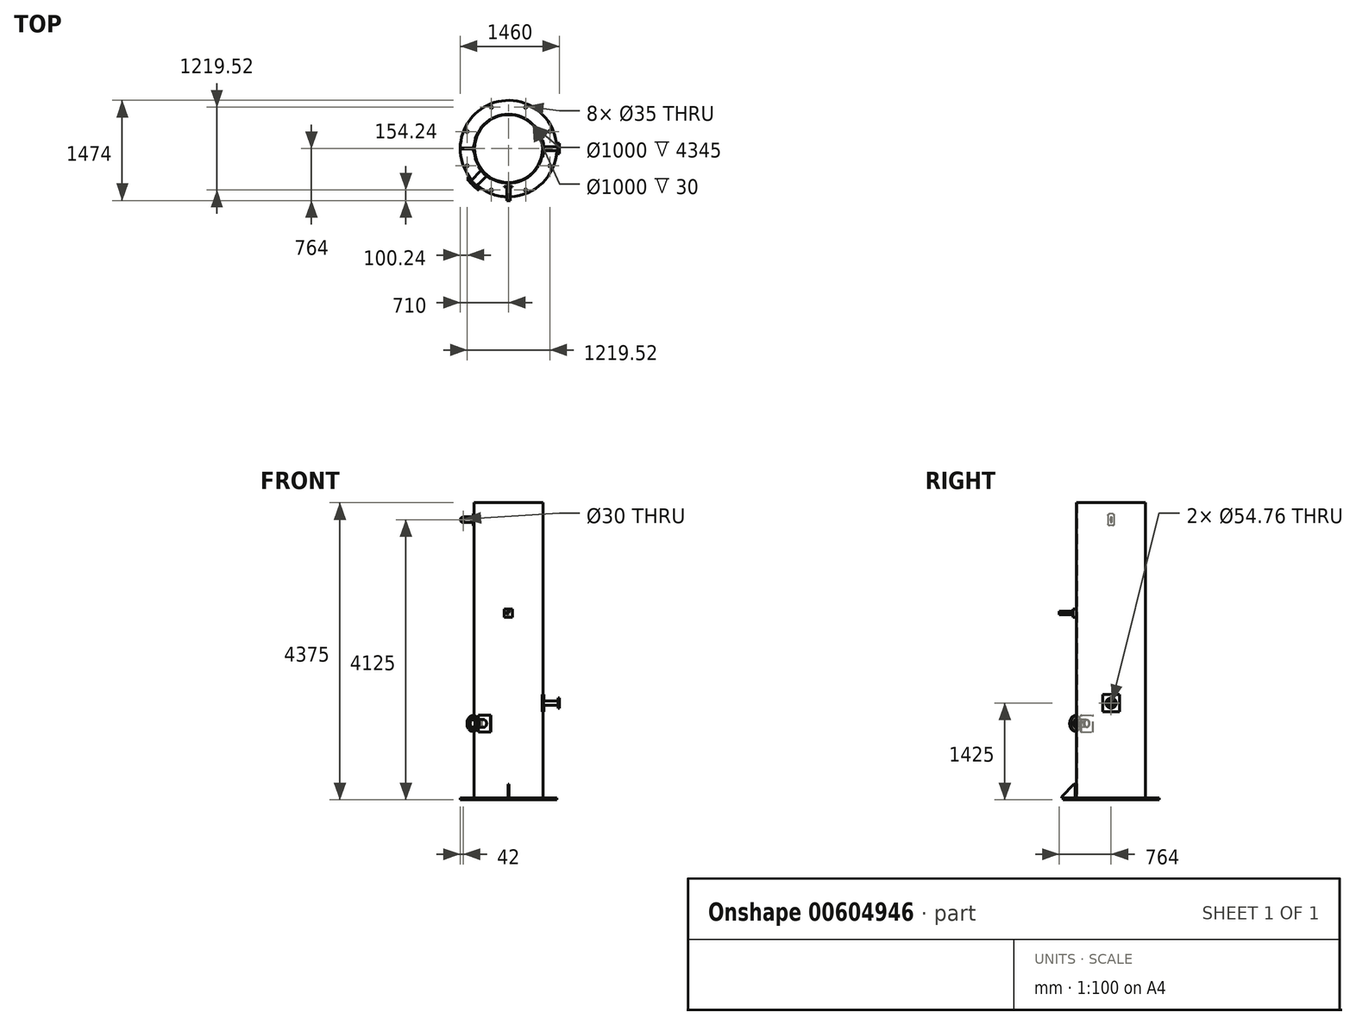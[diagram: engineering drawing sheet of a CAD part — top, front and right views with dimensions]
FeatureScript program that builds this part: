
annotation { "Feature Type Name" : "Feature", "Feature Type Description" : "" }
export const myFeature = defineFeature(function(context is Context, id is Id, definition is map)
    precondition{}
    {
        {
            var Q0;
            Q0=qCreatedBy(makeId("Top.planeOp"),FACE);
            var sketch = newSketch(context, id + "F0", { "sketchPlane" : qUnion([Q0])});
            skCircle(sketch, "E0", {"center": v(0, 0) * mm, "radius": 710 * mm});
            skCircle(sketch, "E1", {"center": v(0, 0) * mm, "radius": 660 * mm, "construction": true});
            skCircle(sketch, "E2", {"center": v(-609.76, 252.57) * mm, "radius": 17.5 * mm});
            skCircle(sketch, "E3.1.0", {"center": v(-252.57, 609.76) * mm, "radius": 17.5 * mm});
            skCircle(sketch, "E3.2.0", {"center": v(252.57, 609.76) * mm, "radius": 17.5 * mm});
            skCircle(sketch, "E3.3.0", {"center": v(609.76, 252.57) * mm, "radius": 17.5 * mm});
            skCircle(sketch, "E3.4.0", {"center": v(609.76, -252.57) * mm, "radius": 17.5 * mm});
            skCircle(sketch, "E3.5.0", {"center": v(252.57, -609.76) * mm, "radius": 17.5 * mm});
            skCircle(sketch, "E3.6.0", {"center": v(-252.57, -609.76) * mm, "radius": 17.5 * mm});
            skCircle(sketch, "E3.7.0", {"center": v(-609.76, -252.57) * mm, "radius": 17.5 * mm});
            skLineSegment(sketch, "E3.anchor1", {"start": v(0, 0) * mm, "end": v(-609.76, 252.57) * mm, "construction": true});
            skLineSegment(sketch, "E3.anchor2", {"start": v(0, 0) * mm, "end": v(-609.76, -252.57) * mm, "construction": true});
            skCircle(sketch, "E4", {"center": v(0, 0) * mm, "radius": 500 * mm});
            skSolve(sketch);
        }
        {
            var Q0;
            Q0=makeQuery(id+"F0.imprint","IMPRINT",FACE,{"disambiguationData":[TD([[makeQuery(id+"F0.imprint","IMPRINT",EDGE,{"derivedFrom":sQuery(id+"F0.wireOp",EDGE,"E0")}),1.0]])]});
            extrude(context, id + "F1", {"entities" : qUnion([Q0]), "depth" : 30 * mm, "offsetDistance" : 25 * mm});
        }
        {
            var Q0;
            Q0=makeQuery(id+"F1.opExtrude","CAP_FACE",FACE,{"disambiguationData":[OSD([sQuery(id+"F0.wireOp",EDGE,"E0"),sQuery(id+"F0.wireOp",EDGE,"E2"),sQuery(id+"F0.wireOp",EDGE,"E3.1.0"),sQuery(id+"F0.wireOp",EDGE,"E3.2.0"),sQuery(id+"F0.wireOp",EDGE,"E3.3.0"),sQuery(id+"F0.wireOp",EDGE,"E3.4.0"),sQuery(id+"F0.wireOp",EDGE,"E3.5.0"),sQuery(id+"F0.wireOp",EDGE,"E3.6.0"),sQuery(id+"F0.wireOp",EDGE,"E3.7.0"),sQuery(id+"F0.wireOp",EDGE,"E4")])],"isStart":false});
            var sketch = newSketch(context, id + "F2", { "sketchPlane" : qUnion([Q0])});
            skCircle(sketch, "E5", {"center": v(0, 0) * mm, "radius": 508 * mm});
            skCircle(sketch, "E6", {"center": v(0, 0) * mm, "radius": 498.5 * mm});
            skSolve(sketch);
        }
        {
            var Q0;
            Q0=makeQuery(id+"F2.imprint","IMPRINT",FACE,{"disambiguationData":[TD([[makeQuery(id+"F2.imprint","IMPRINT",EDGE,{"derivedFrom":sQuery(id+"F2.wireOp",EDGE,"E5")}),1.0]])]});
            extrude(context, id + "F3", {"entities" : qUnion([Q0]), "depth" : (4375 - 30) * mm, "offsetDistance" : 25 * mm});
        }
        {
            var Q0;
            Q0=makeQuery(id+"F1.opExtrude","CAP_FACE",FACE,{"disambiguationData":[OSD([sQuery(id+"F0.wireOp",EDGE,"E0"),sQuery(id+"F0.wireOp",EDGE,"E2"),sQuery(id+"F0.wireOp",EDGE,"E3.1.0"),sQuery(id+"F0.wireOp",EDGE,"E3.2.0"),sQuery(id+"F0.wireOp",EDGE,"E3.3.0"),sQuery(id+"F0.wireOp",EDGE,"E3.4.0"),sQuery(id+"F0.wireOp",EDGE,"E3.5.0"),sQuery(id+"F0.wireOp",EDGE,"E3.6.0"),sQuery(id+"F0.wireOp",EDGE,"E3.7.0"),sQuery(id+"F0.wireOp",EDGE,"E4")])],"isStart":true});
            cPlane(context, id + "F4", {"entities" : qUnion([Q0]), "cplaneType" : CPlaneType.OFFSET, "offset" : 1125 * mm, "oppositeDirection" : true, "width" : 150 * mm, "height" : 150 * mm});
        }
        {
            var Q0;
            Q0=qCreatedBy(id+"F4.planeOp",FACE);
            var sketch = newSketch(context, id + "F5", { "sketchPlane" : qUnion([Q0])});
            skCircle(sketch, "E7", {"center": v(0, 0) * mm, "radius": 508 * mm});
            skCircle(sketch, "E8", {"center": v(0, 0) * mm, "radius": 518 * mm});
            skLineSegment(sketch, "E9", {"start": v(0, 0) * mm, "end": v(-443.85, 267.07) * mm});
            skLineSegment(sketch, "E10", {"start": v(0, 0) * mm, "end": v(-267.07, 443.85) * mm});
            skLineSegment(sketch, "E11", {"start": v(-443.85, 267.07) * mm, "end": v(-267.07, 443.85) * mm, "construction": true});
            skLineSegment(sketch, "E12", {"start": v(0, 0) * mm, "end": v(502.7, -125) * mm});
            skLineSegment(sketch, "E13", {"start": v(0, 0) * mm, "end": v(502.7, 125) * mm});
            skLineSegment(sketch, "E14", {"start": v(502.7, 125) * mm, "end": v(502.7, -125) * mm, "construction": true});
            skLineSegment(sketch, "E15", {"start": v(0, 0) * mm, "end": v(750, 0) * mm, "construction": true});
            skLineSegment(sketch, "E16", {"start": v(750, 0) * mm, "end": v(750, -75) * mm});
            skLineSegment(sketch, "E17", {"start": v(750, -75) * mm, "end": v(730.9, -75) * mm});
            skLineSegment(sketch, "E18", {"start": v(730.9, -75) * mm, "end": v(730.9, -30.15) * mm});
            skLineSegment(sketch, "E19", {"start": v(730.9, -30.15) * mm, "end": v(517.12, -30.15) * mm});
            skLineSegment(sketch, "E20", {"start": v(750, -27.38) * mm, "end": v(517.28, -27.38) * mm});
            skLineSegment(sketch, "E21", {"start": v(748.4, -75) * mm, "end": v(748.4, -45.95) * mm});
            skLineSegment(sketch, "E22", {"start": v(748.4, -45.95) * mm, "end": v(750, -45.95) * mm});
            skSolve(sketch);
        }
        {
            var Q0;
            {var subQ0=sQuery(id+"F5.wireOp",EDGE,"E9");var subQ1=sQuery(id+"F5.wireOp",EDGE,"E7");var subQ2=makeQuery(id+"F5.imprint","INTERSECT",VERTEX,{"derivedFrom":[subQ1,subQ0]});Q0=makeQuery(id+"F5.imprint","IMPRINT",FACE,{"disambiguationData":[TD([[makeQuery(id+"F5.imprint","IMPRINT",EDGE,{"disambiguationData":[TD([[subQ2,1.0]])],"derivedFrom":subQ1}),-1.0]])]});}
            extrude(context, id + "F6", {"entities" : qUnion([Q0]), "endBound" : BoundingType.SYMMETRIC, "depth" : 250 * mm, "offsetDistance" : 25 * mm});
        }
        {
            var Q0;
            Q0=qCreatedBy(makeId("Right.planeOp"),FACE);
            var sketch = newSketch(context, id + "F7", { "sketchPlane" : qUnion([Q0])});
            skLineSegment(sketch, "E23.bottom", {"start": v(-527.24, 30) * mm, "end": v(-727.24, 30) * mm});
            skLineSegment(sketch, "E23.top", {"start": v(-527.24, 230) * mm, "end": v(-727.24, 230) * mm});
            skLineSegment(sketch, "E23.left", {"start": v(-527.24, 30) * mm, "end": v(-527.24, 230) * mm});
            skLineSegment(sketch, "E23.right", {"start": v(-727.24, 30) * mm, "end": v(-727.24, 230) * mm});
            skLineSegment(sketch, "E24", {"start": v(0, 2750) * mm, "end": v(-631.56, 2750) * mm, "construction": true});
            skLineSegment(sketch, "E25.bottom", {"start": v(-508, 2810) * mm, "end": v(-558, 2810) * mm});
            skLineSegment(sketch, "E25.top", {"start": v(-508, 2690) * mm, "end": v(-558, 2690) * mm});
            skLineSegment(sketch, "E25.left", {"start": v(-508, 2810) * mm, "end": v(-508, 2690) * mm});
            skLineSegment(sketch, "E25.right", {"start": v(-558, 2810) * mm, "end": v(-558, 2690) * mm});
            skPoint(sketch, "E25.middle", {"position": v(-533, 2750) * mm});
            skLineSegment(sketch, "E26.bottom", {"start": v(-558, 2810) * mm, "end": v(-564, 2810) * mm});
            skLineSegment(sketch, "E26.top", {"start": v(-558, 2690) * mm, "end": v(-564, 2690) * mm});
            skLineSegment(sketch, "E26.right", {"start": v(-564, 2810) * mm, "end": v(-564, 2690) * mm});
            skPoint(sketch, "E26.middle", {"position": v(-561, 2750) * mm});
            skSolve(sketch);
        }
        {
            var Q0;
            Q0=makeQuery(id+"F7.imprint","IMPRINT",FACE,{"disambiguationData":[TD([[makeQuery(id+"F7.imprint","IMPRINT",EDGE,{"derivedFrom":sQuery(id+"F7.wireOp",EDGE,"E23.bottom")}),-1.0]])]});
            extrude(context, id + "F8", {"entities" : qUnion([Q0]), "endBound" : BoundingType.SYMMETRIC, "oppositeDirection" : true, "depth" : 10 * mm, "offsetDistance" : 25 * mm});
        }
        {
            var Q0;
            Q0=makeQuery(id+"F8.opExtrude","SWEPT_EDGE",EDGE,{"disambiguationData":[OSD([sQuery(id+"F7.wireOp",EDGE,"E23.top"),sQuery(id+"F7.wireOp",EDGE,"E23.right")])]});
            chamfer(context, id + "F9", {"entities" : qUnion([Q0]), "width" : 180 * mm, "tangentPropagation" : true});
        }
        {
            var Q0;
            Q0=qCreatedBy(makeId("Right.planeOp"),FACE);
            var Q1;
            Q1=makeQuery(id+"F3.opExtrude","SWEPT_FACE",FACE,{"disambiguationData":[OSD([sQuery(id+"F2.wireOp",EDGE,"E5")])]});
            cPlane(context, id + "F10", {"entities" : qUnion([Q0, Q1]), "cplaneType" : CPlaneType.LINE_ANGLE, "offset" : 25 * mm, "angle" : 45 * degree, "width" : 150 * mm, "height" : 150 * mm});
        }
        {
            var Q0;
            Q0=qCreatedBy(id+"F10.planeOp",FACE);
            var sketch = newSketch(context, id + "F11", { "sketchPlane" : qUnion([Q0])});
            skLineSegment(sketch, "E27", {"start": v(515.95, 1182.15) * mm, "end": v(726.1, 1182.15) * mm});
            skLineSegment(sketch, "E28", {"start": v(726.1, 1182.15) * mm, "end": v(726.1, 1240) * mm});
            skLineSegment(sketch, "E29", {"start": v(726.1, 1240) * mm, "end": v(748.4, 1240) * mm});
            skLineSegment(sketch, "E30", {"start": v(750, 1240) * mm, "end": v(750, 1203.6) * mm, "construction": true});
            skLineSegment(sketch, "E31", {"start": v(750, 1125) * mm, "end": v(515.95, 1125) * mm, "construction": true});
            skLineSegment(sketch, "E32", {"start": v(515.95, 1125) * mm, "end": v(515.95, 1182.15) * mm});
            skLineSegment(sketch, "E33", {"start": v(750, 1179.1) * mm, "end": v(515.95, 1179.1) * mm});
            skLineSegment(sketch, "E34", {"start": v(750, 1203.6) * mm, "end": v(748.4, 1203.6) * mm});
            skLineSegment(sketch, "E35", {"start": v(748.4, 1203.6) * mm, "end": v(748.4, 1240) * mm});
            skLineSegment(sketch, "E36", {"start": v(750, 1203.6) * mm, "end": v(750, 1125) * mm});
            skLineSegment(sketch, "E37", {"start": v(748.4, 1240) * mm, "end": v(750, 1240) * mm, "construction": true});
            skSolve(sketch);
        }
        {
            var Q0;
            {var subQ3=sQuery(id+"F11.wireOp",EDGE,"E27");Q0=makeQuery(id+"F11.imprint","IMPRINT",FACE,{"disambiguationData":[TD([[makeQuery(id+"F11.imprint","IMPRINT",EDGE,{"derivedFrom":subQ3}),-1.0]])]});}
            var Q1;
            Q1=sQuery(id+"F11.wireOp",EDGE,"E31");
            revolve(context, id + "F12", {"operationType" : NewBodyOperationType.ADD, "entities" : qUnion([Q0]), "axis" : qUnion([Q1]), "revolveType" : RevolveType.FULL});
        }
        {
            var Q0;
            Q0=makeQuery(id+"F12.opRevolve","SWEPT_FACE",FACE,{"disambiguationData":[OSD([sQuery(id+"F11.wireOp",EDGE,"E36")])]});
            var sketch = newSketch(context, id + "F13", { "sketchPlane" : qUnion([Q0])});
            skCircle(sketch, "E38.0", {"center": v(0, 1125) * mm, "radius": 54.1 * mm});
            skSolve(sketch);
        }
        {
            var Q0;
            Q0=makeQuery(id+"F13.imprint","IMPRINT",FACE,{"disambiguationData":[TD([[makeQuery(id+"F13.imprint","IMPRINT",EDGE,{"derivedFrom":sQuery(id+"F13.wireOp",EDGE,"E38.0")}),1.0]])]});
            extrude(context, id + "F14", {"entities" : qUnion([Q0]), "operationType" : NewBodyOperationType.REMOVE, "oppositeDirection" : true, "depth" : 500 * mm, "offsetDistance" : 25 * mm});
        }
        {
            var Q0;
            Q0=qCreatedBy(id+"F4.planeOp",FACE);
            cPlane(context, id + "F15", {"entities" : qUnion([Q0]), "cplaneType" : CPlaneType.OFFSET, "offset" : 300 * mm, "oppositeDirection" : true, "width" : 150 * mm, "height" : 150 * mm});
        }
        {
            var Q0;
            Q0=qCreatedBy(id+"F15.planeOp",FACE);
            var sketch = newSketch(context, id + "F16", { "sketchPlane" : qUnion([Q0])});
            skCircle(sketch, "E39", {"center": v(0, 0) * mm, "radius": 508 * mm});
            skCircle(sketch, "E40", {"center": v(0, 0) * mm, "radius": 518 * mm});
            skLineSegment(sketch, "E41", {"start": v(0, 0) * mm, "end": v(502.7, -125) * mm});
            skLineSegment(sketch, "E42", {"start": v(0, 0) * mm, "end": v(502.7, 125) * mm});
            skLineSegment(sketch, "E43", {"start": v(502.7, 125) * mm, "end": v(502.7, -125) * mm, "construction": true});
            skLineSegment(sketch, "E44", {"start": v(0, 0) * mm, "end": v(750, 0) * mm, "construction": true});
            skLineSegment(sketch, "E45", {"start": v(750, 0) * mm, "end": v(750, -75) * mm});
            skLineSegment(sketch, "E46", {"start": v(750, -75) * mm, "end": v(730.9, -75) * mm});
            skLineSegment(sketch, "E47", {"start": v(730.9, -75) * mm, "end": v(730.9, -30.15) * mm});
            skLineSegment(sketch, "E48", {"start": v(730.9, -30.15) * mm, "end": v(517.12, -30.15) * mm});
            skLineSegment(sketch, "E49", {"start": v(750, -27.38) * mm, "end": v(517.28, -27.38) * mm});
            skLineSegment(sketch, "E50", {"start": v(748.4, -75) * mm, "end": v(748.4, -45.95) * mm});
            skLineSegment(sketch, "E51", {"start": v(748.4, -45.95) * mm, "end": v(750, -45.95) * mm});
            skSolve(sketch);
        }
        {
            var Q0;
            {var subQ5=sQuery(id+"F16.wireOp",EDGE,"E41");var subQ7=sQuery(id+"F16.wireOp",EDGE,"E39");var subQ8=makeQuery(id+"F16.imprint","INTERSECT",VERTEX,{"derivedFrom":[subQ7,subQ5]});Q0=makeQuery(id+"F16.imprint","IMPRINT",FACE,{"disambiguationData":[TD([[makeQuery(id+"F16.imprint","IMPRINT",EDGE,{"disambiguationData":[TD([[subQ8,-1.0]])],"derivedFrom":subQ7}),-1.0]])]});}
            extrude(context, id + "F17", {"entities" : qUnion([Q0]), "endBound" : BoundingType.SYMMETRIC, "depth" : 250 * mm, "offsetDistance" : 25 * mm});
        }
        {
            var Q0;
            {var subQ0=sQuery(id+"F16.wireOp",EDGE,"E47");Q0=makeQuery(id+"F16.imprint","IMPRINT",FACE,{"disambiguationData":[TD([[makeQuery(id+"F16.imprint","IMPRINT",EDGE,{"derivedFrom":subQ0}),-1.0]])]});}
            var Q1;
            Q1=sQuery(id+"F16.wireOp",EDGE,"E44");
            revolve(context, id + "F18", {"operationType" : NewBodyOperationType.ADD, "entities" : qUnion([Q0]), "axis" : qUnion([Q1]), "revolveType" : RevolveType.FULL});
        }
        {
            var Q0;
            Q0=makeQuery(id+"F18.opRevolve","SWEPT_FACE",FACE,{"disambiguationData":[OSD([sQuery(id+"F16.wireOp",EDGE,"E45")])]});
            var sketch = newSketch(context, id + "F19", { "sketchPlane" : qUnion([Q0])});
            skCircle(sketch, "E52.0", {"center": v(0, 1425) * mm, "radius": 27.38 * mm});
            skSolve(sketch);
        }
        {
            var Q0;
            Q0 = qSketchRegion(id + "F19", true);
            extrude(context, id + "F20", {"entities" : qUnion([Q0]), "operationType" : NewBodyOperationType.REMOVE, "oppositeDirection" : true, "depth" : 500 * mm, "offsetDistance" : 25 * mm});
        }
        {
            var Q0;
            Q0=makeQuery(id+"F3.opExtrude","CAP_FACE",FACE,{"disambiguationData":[OSD([sQuery(id+"F0.wireOp",EDGE,"E4"),sQuery(id+"F2.wireOp",EDGE,"E5")])],"isStart":false});
            cPlane(context, id + "F21", {"entities" : qUnion([Q0]), "cplaneType" : CPlaneType.OFFSET, "offset" : 250 * mm, "oppositeDirection" : true, "width" : 150 * mm, "height" : 150 * mm});
        }
        {
            var Q0;
            Q0=qCreatedBy(id+"F21.planeOp",FACE);
            var sketch = newSketch(context, id + "F22", { "sketchPlane" : qUnion([Q0])});
            skCircle(sketch, "E53.0", {"center": v(0, 0) * mm, "radius": 508 * mm});
            skLineSegment(sketch, "E54", {"start": v(0, 0) * mm, "end": v(-516.04, 45) * mm});
            skLineSegment(sketch, "E55", {"start": v(-516.04, 45) * mm, "end": v(-516.04, -45) * mm, "construction": true});
            skLineSegment(sketch, "E56", {"start": v(-516.04, -45) * mm, "end": v(0, 0) * mm});
            skCircle(sketch, "E57", {"center": v(0, 0) * mm, "radius": 518 * mm});
            skSolve(sketch);
        }
        {
            var Q0;
            {var subQ0=sQuery(id+"F22.wireOp",EDGE,"E54");var subQ1=sQuery(id+"F22.wireOp",EDGE,"E53.0");var subQ2=makeQuery(id+"F22.imprint","INTERSECT",VERTEX,{"derivedFrom":[subQ1,subQ0]});Q0=makeQuery(id+"F22.imprint","IMPRINT",FACE,{"disambiguationData":[TD([[makeQuery(id+"F22.imprint","IMPRINT",EDGE,{"disambiguationData":[TD([[subQ2,-1.0]])],"derivedFrom":subQ1}),-1.0]])]});}
            extrude(context, id + "F23", {"entities" : qUnion([Q0]), "endBound" : BoundingType.SYMMETRIC, "depth" : 170 * mm, "offsetDistance" : 25 * mm});
        }
        {
            var Q0;
            Q0=qCreatedBy(makeId("Front.planeOp"),FACE);
            var sketch = newSketch(context, id + "F24", { "sketchPlane" : qUnion([Q0])});
            skLineSegment(sketch, "E58", {"start": v(-843.58, 4125) * mm, "end": v(-316.92, 4125) * mm, "construction": true});
            skLineSegment(sketch, "E59.bottom", {"start": v(-508, 4165) * mm, "end": v(-518, 4165) * mm});
            skLineSegment(sketch, "E59.top", {"start": v(-508, 4085) * mm, "end": v(-518, 4085) * mm});
            skLineSegment(sketch, "E59.left", {"start": v(-508, 4165) * mm, "end": v(-508, 4085) * mm});
            skLineSegment(sketch, "E59.right", {"start": v(-518, 4165) * mm, "end": v(-518, 4085) * mm});
            skPoint(sketch, "E59.middle", {"position": v(-513, 4125) * mm});
            skLineSegment(sketch, "E60.bottom", {"start": v(-518, 4165) * mm, "end": v(-668, 4165) * mm});
            skLineSegment(sketch, "E60.top", {"start": v(-518, 4085) * mm, "end": v(-668, 4085) * mm});
            skLineSegment(sketch, "E60.right", {"start": v(-708, 4125) * mm, "end": v(-708, 4125) * mm});
            skPoint(sketch, "E60.middle", {"position": v(-613, 4125) * mm});
            skPoint(sketch, "E61.visualSharp", {"position": v(-708, 4165) * mm});
            skArc(sketch, "E61.filletArc", {"start": v(-668, 4165) * mm, "mid": v(-696.28, 4153.28) * mm, "end": v(-708, 4125) * mm});
            skPoint(sketch, "E62.visualSharp", {"position": v(-708, 4085) * mm});
            skArc(sketch, "E62.filletArc", {"start": v(-708, 4125) * mm, "mid": v(-696.28, 4096.72) * mm, "end": v(-668, 4085) * mm});
            skCircle(sketch, "E63", {"center": v(-668, 4125) * mm, "radius": 15 * mm});
            skSolve(sketch);
        }
        {
            var Q0;
            Q0=makeQuery(id+"F24.imprint","IMPRINT",FACE,{"disambiguationData":[TD([[makeQuery(id+"F24.imprint","IMPRINT",EDGE,{"derivedFrom":sQuery(id+"F24.wireOp",EDGE,"E60.bottom")}),1.0]])]});
            var Q1;
            Q1=makeQuery(id+"F24.imprint","IMPRINT",FACE,{"disambiguationData":[TD([[makeQuery(id+"F24.imprint","IMPRINT",EDGE,{"derivedFrom":sQuery(id+"F24.wireOp",EDGE,"E59.bottom")}),1.0]])]});
            extrude(context, id + "F25", {"entities" : qUnion([Q0, Q1]), "operationType" : NewBodyOperationType.ADD, "endBound" : BoundingType.SYMMETRIC, "depth" : 15 * mm, "offsetDistance" : 25 * mm});
        }
        {
            var Q0;
            Q0=makeQuery(id+"F7.imprint","IMPRINT",FACE,{"disambiguationData":[TD([[makeQuery(id+"F7.imprint","IMPRINT",EDGE,{"derivedFrom":sQuery(id+"F7.wireOp",EDGE,"E25.bottom")}),1.0]])]});
            extrude(context, id + "F26", {"entities" : qUnion([Q0]), "endBound" : BoundingType.SYMMETRIC, "depth" : 6 * mm, "offsetDistance" : 25 * mm});
        }
        {
            var Q0;
            Q0=makeQuery(id+"F7.imprint","IMPRINT",FACE,{"disambiguationData":[TD([[makeQuery(id+"F7.imprint","IMPRINT",EDGE,{"derivedFrom":sQuery(id+"F7.wireOp",EDGE,"E26.bottom")}),1.0]])]});
            extrude(context, id + "F27", {"entities" : qUnion([Q0]), "operationType" : NewBodyOperationType.ADD, "endBound" : BoundingType.SYMMETRIC, "depth" : 120 * mm, "offsetDistance" : 25 * mm});
        }
        {
            var Q0;
            Q0=makeQuery(id+"F27.opExtrude","SWEPT_FACE",FACE,{"disambiguationData":[OSD([sQuery(id+"F7.wireOp",EDGE,"E26.right")])]});
            var sketch = newSketch(context, id + "F28", { "sketchPlane" : qUnion([Q0])});
            skLineSegment(sketch, "E64", {"start": v(-25, 2725) * mm, "end": v(-25, 2775) * mm});
            skLineSegment(sketch, "E65", {"start": v(-25, 2775) * mm, "end": v(25, 2775) * mm});
            skLineSegment(sketch, "E66", {"start": v(25, 2775) * mm, "end": v(25, 2770) * mm});
            skLineSegment(sketch, "E67", {"start": v(25, 2770) * mm, "end": v(-20, 2770) * mm});
            skLineSegment(sketch, "E68", {"start": v(-20, 2770) * mm, "end": v(-20, 2725) * mm});
            skLineSegment(sketch, "E69", {"start": v(-20, 2725) * mm, "end": v(-25, 2725) * mm});
            skSolve(sketch);
        }
        {
            var Q0;
            Q0=makeQuery(id+"F28.imprint","IMPRINT",FACE,{"disambiguationData":[TD([[makeQuery(id+"F28.imprint","IMPRINT",EDGE,{"derivedFrom":sQuery(id+"F28.wireOp",EDGE,"E64")}),-1.0]])]});
            extrude(context, id + "F29", {"entities" : qUnion([Q0]), "operationType" : NewBodyOperationType.ADD, "depth" : 200 * mm, "offsetDistance" : 25 * mm});
        }
        {
            var Q0;
            Q0=makeQuery(id+"F23.opExtrude","CAP_EDGE",EDGE,{"disambiguationData":[OSD([sQuery(id+"F22.wireOp",EDGE,"E56")])],"isStart":false});
            var Q1;
            Q1=makeQuery(id+"F23.opExtrude","CAP_EDGE",EDGE,{"disambiguationData":[OSD([sQuery(id+"F22.wireOp",EDGE,"E54")])],"isStart":false});
            var Q2;
            Q2=makeQuery(id+"F23.opExtrude","CAP_EDGE",EDGE,{"disambiguationData":[OSD([sQuery(id+"F22.wireOp",EDGE,"E56")])],"isStart":true});
            var Q3;
            Q3=makeQuery(id+"F23.opExtrude","CAP_EDGE",EDGE,{"disambiguationData":[OSD([sQuery(id+"F22.wireOp",EDGE,"E54")])],"isStart":true});
            fillet(context, id + "F30", {"entities" : qUnion([Q0, Q1, Q2, Q3]), "radius" : 20 * mm, "tangentPropagation" : true, "allowEdgeOverflow" : false});
        }
    });
